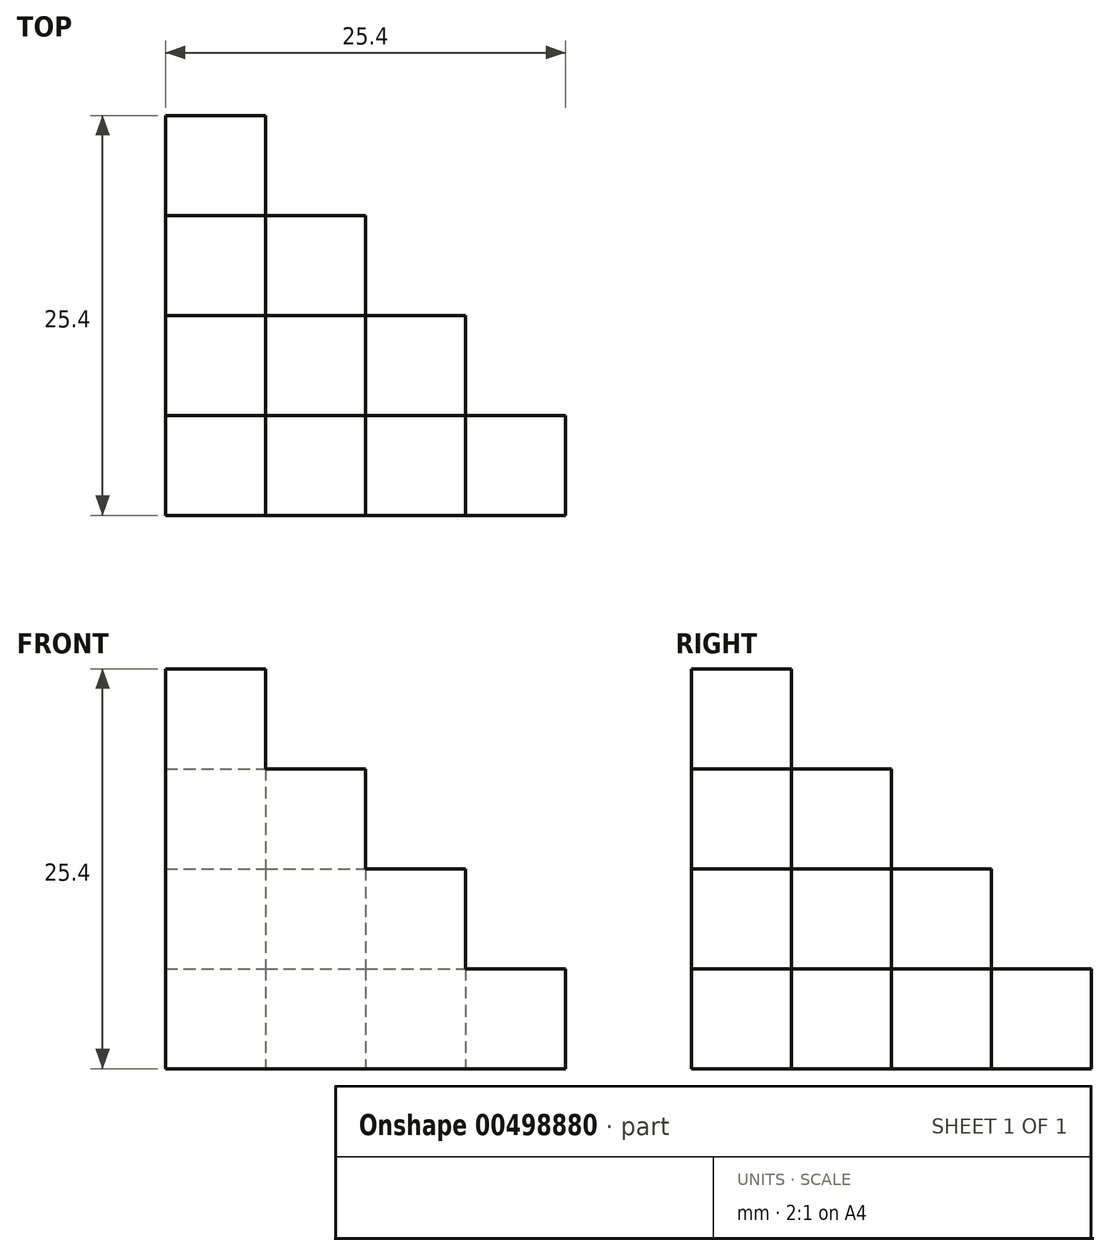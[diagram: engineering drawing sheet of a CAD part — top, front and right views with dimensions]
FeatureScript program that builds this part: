
annotation { "Feature Type Name" : "Feature", "Feature Type Description" : "" }
export const myFeature = defineFeature(function(context is Context, id is Id, definition is map)
    precondition{}
    {
        {
            var Q0;
            Q0=qCreatedBy(makeId("Top.planeOp"),FACE);
            var sketch = newSketch(context, id + "F0", { "sketchPlane" : qUnion([Q0])});
            skLineSegment(sketch, "E0.top", {"start": v(0, -25.4) * mm, "end": v(25.4, -25.4) * mm});
            skLineSegment(sketch, "E0.left", {"start": v(0, 0) * mm, "end": v(0, -25.4) * mm});
            skLineSegment(sketch, "E1", {"start": v(0, 0) * mm, "end": v(6.35, 0) * mm});
            skLineSegment(sketch, "E2", {"start": v(6.35, 0) * mm, "end": v(6.35, -6.35) * mm});
            skLineSegment(sketch, "E3", {"start": v(6.35, -6.35) * mm, "end": v(12.7, -6.35) * mm});
            skLineSegment(sketch, "E4", {"start": v(12.7, -6.35) * mm, "end": v(12.7, -12.7) * mm});
            skLineSegment(sketch, "E5", {"start": v(12.7, -12.7) * mm, "end": v(19.05, -12.7) * mm});
            skLineSegment(sketch, "E6", {"start": v(19.05, -12.7) * mm, "end": v(19.05, -19.05) * mm});
            skLineSegment(sketch, "E7", {"start": v(19.05, -19.05) * mm, "end": v(25.4, -19.05) * mm});
            skLineSegment(sketch, "E8", {"start": v(25.4, -19.05) * mm, "end": v(25.4, -25.4) * mm});
            skSolve(sketch);
        }
        {
            var Q0;
            Q0=makeQuery(id+"F0.imprint","IMPRINT",FACE,{"disambiguationData":[TD([[makeQuery(id+"F0.imprint","IMPRINT",EDGE,{"derivedFrom":sQuery(id+"F0.wireOp",EDGE,"E0.top")}),1.0]])]});
            extrude(context, id + "F1", {"entities" : qUnion([Q0]), "depth" : 6.35 * mm});
        }
        {
            var Q0;
            Q0=makeQuery(id+"F1.opExtrude","CAP_FACE",FACE,{"disambiguationData":[OSD([sQuery(id+"F0.wireOp",EDGE,"E0.top"),sQuery(id+"F0.wireOp",EDGE,"E0.left"),sQuery(id+"F0.wireOp",EDGE,"E1"),sQuery(id+"F0.wireOp",EDGE,"E2"),sQuery(id+"F0.wireOp",EDGE,"E3"),sQuery(id+"F0.wireOp",EDGE,"E4"),sQuery(id+"F0.wireOp",EDGE,"E5"),sQuery(id+"F0.wireOp",EDGE,"E6"),sQuery(id+"F0.wireOp",EDGE,"E7"),sQuery(id+"F0.wireOp",EDGE,"E8")])],"isStart":false});
            var sketch = newSketch(context, id + "F2", { "sketchPlane" : qUnion([Q0])});
            skLineSegment(sketch, "E9", {"start": v(0, -6.35) * mm, "end": v(6.35, -6.35) * mm});
            skLineSegment(sketch, "E10", {"start": v(6.35, -6.35) * mm, "end": v(6.35, -12.7) * mm});
            skLineSegment(sketch, "E11", {"start": v(6.35, -12.7) * mm, "end": v(12.7, -12.7) * mm});
            skLineSegment(sketch, "E12", {"start": v(12.7, -12.7) * mm, "end": v(12.7, -19.05) * mm});
            skLineSegment(sketch, "E13", {"start": v(12.7, -19.05) * mm, "end": v(19.05, -19.05) * mm});
            skLineSegment(sketch, "E14", {"start": v(19.05, -19.05) * mm, "end": v(19.05, -25.4) * mm});
            skLineSegment(sketch, "E15", {"start": v(19.05, -25.4) * mm, "end": v(0, -25.4) * mm});
            skLineSegment(sketch, "E16", {"start": v(0, -25.4) * mm, "end": v(0, -6.35) * mm});
            skSolve(sketch);
        }
        {
            var Q0;
            Q0=makeQuery(id+"F2.imprint","IMPRINT",FACE,{"disambiguationData":[TD([[makeQuery(id+"F2.imprint","IMPRINT",EDGE,{"derivedFrom":sQuery(id+"F2.wireOp",EDGE,"E9")}),-1.0]])]});
            extrude(context, id + "F3", {"entities" : qUnion([Q0]), "operationType" : NewBodyOperationType.ADD, "depth" : 6.35 * mm});
        }
        {
            var Q0;
            Q0=makeQuery(id+"F3.opExtrude","CAP_FACE",FACE,{"disambiguationData":[OSD([sQuery(id+"F2.wireOp",EDGE,"E9"),sQuery(id+"F2.wireOp",EDGE,"E10"),sQuery(id+"F2.wireOp",EDGE,"E11"),sQuery(id+"F2.wireOp",EDGE,"E12"),sQuery(id+"F2.wireOp",EDGE,"E13"),sQuery(id+"F2.wireOp",EDGE,"E14"),sQuery(id+"F2.wireOp",EDGE,"E15"),sQuery(id+"F2.wireOp",EDGE,"E16")])],"isStart":false});
            var sketch = newSketch(context, id + "F4", { "sketchPlane" : qUnion([Q0])});
            skLineSegment(sketch, "E17", {"start": v(0, -12.7) * mm, "end": v(6.35, -12.7) * mm});
            skLineSegment(sketch, "E18", {"start": v(6.35, -12.7) * mm, "end": v(6.35, -19.05) * mm});
            skLineSegment(sketch, "E19", {"start": v(6.35, -19.05) * mm, "end": v(12.7, -19.05) * mm});
            skLineSegment(sketch, "E20", {"start": v(12.7, -19.05) * mm, "end": v(12.7, -25.4) * mm});
            skLineSegment(sketch, "E21", {"start": v(12.7, -25.4) * mm, "end": v(0, -25.4) * mm});
            skLineSegment(sketch, "E22", {"start": v(0, -25.4) * mm, "end": v(0, -12.7) * mm});
            skSolve(sketch);
        }
        {
            var Q0;
            Q0=makeQuery(id+"F4.imprint","IMPRINT",FACE,{"disambiguationData":[TD([[makeQuery(id+"F4.imprint","IMPRINT",EDGE,{"derivedFrom":sQuery(id+"F4.wireOp",EDGE,"E17")}),-1.0]])]});
            extrude(context, id + "F5", {"entities" : qUnion([Q0]), "operationType" : NewBodyOperationType.ADD, "depth" : 6.35 * mm});
        }
        {
            var Q0;
            Q0=makeQuery(id+"F5.opExtrude","CAP_FACE",FACE,{"disambiguationData":[OSD([sQuery(id+"F4.wireOp",EDGE,"E17"),sQuery(id+"F4.wireOp",EDGE,"E18"),sQuery(id+"F4.wireOp",EDGE,"E19"),sQuery(id+"F4.wireOp",EDGE,"E20"),sQuery(id+"F4.wireOp",EDGE,"E21"),sQuery(id+"F4.wireOp",EDGE,"E22")])],"isStart":false});
            var sketch = newSketch(context, id + "F6", { "sketchPlane" : qUnion([Q0])});
            skLineSegment(sketch, "E23", {"start": v(6.35, -19.05) * mm, "end": v(6.35, -25.4) * mm});
            skLineSegment(sketch, "E24", {"start": v(6.35, -25.4) * mm, "end": v(0, -25.4) * mm});
            skLineSegment(sketch, "E25", {"start": v(0, -25.4) * mm, "end": v(0, -19.05) * mm});
            skLineSegment(sketch, "E26", {"start": v(0, -19.05) * mm, "end": v(6.35, -19.05) * mm});
            skSolve(sketch);
        }
        {
            var Q0;
            Q0=makeQuery(id+"F6.imprint","IMPRINT",FACE,{"disambiguationData":[TD([[makeQuery(id+"F6.imprint","IMPRINT",EDGE,{"derivedFrom":sQuery(id+"F6.wireOp",EDGE,"E23")}),-1.0]])]});
            extrude(context, id + "F7", {"entities" : qUnion([Q0]), "operationType" : NewBodyOperationType.ADD, "depth" : 6.35 * mm});
        }
    });
